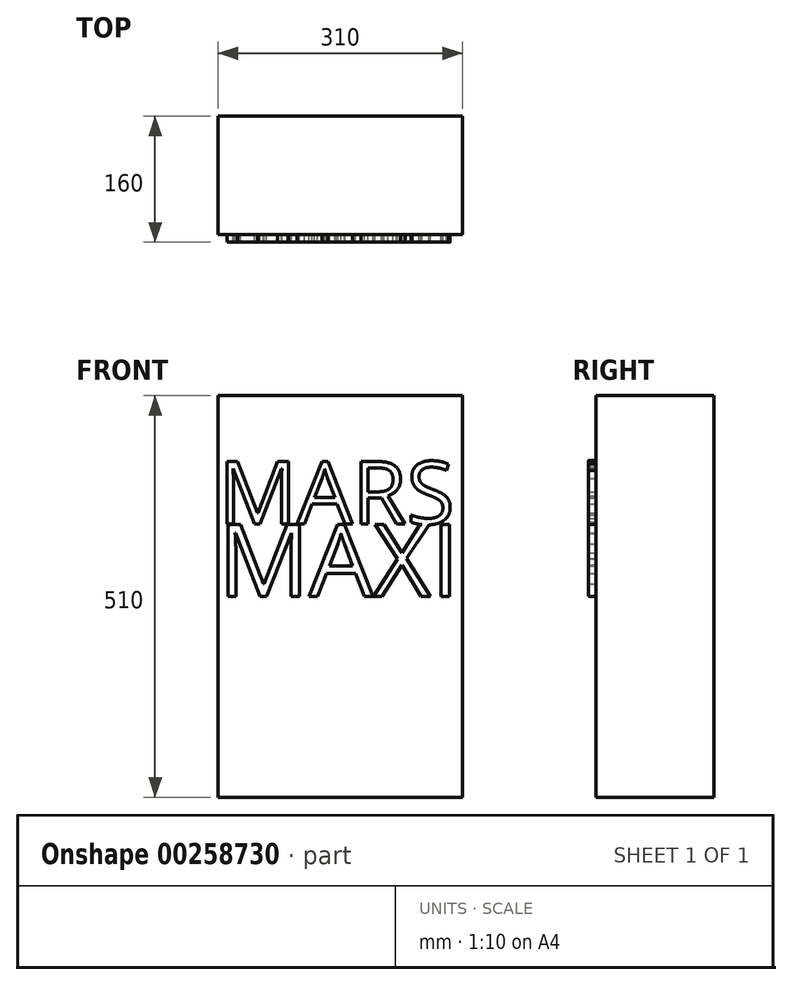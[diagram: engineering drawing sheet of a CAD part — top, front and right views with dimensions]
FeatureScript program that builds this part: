
annotation { "Feature Type Name" : "Feature", "Feature Type Description" : "" }
export const myFeature = defineFeature(function(context is Context, id is Id, definition is map)
    precondition{}
    {
        {
            var Q0;
            Q0=qCreatedBy(makeId("Front.planeOp"),FACE);
            var sketch = newSketch(context, id + "F0", { "sketchPlane" : qUnion([Q0])});
            skLineSegment(sketch, "E0.bottom", {"start": v(0, 0) * mm, "end": v(310, 0) * mm});
            skLineSegment(sketch, "E0.top", {"start": v(0, 510) * mm, "end": v(310, 510) * mm});
            skLineSegment(sketch, "E0.left", {"start": v(0, 0) * mm, "end": v(0, 510) * mm});
            skLineSegment(sketch, "E0.right", {"start": v(310, 0) * mm, "end": v(310, 510) * mm});
            skSolve(sketch);
        }
        {
            var Q0;
            Q0 = qSketchRegion(id + "F0", true);
            var Q1;
            Q1=makeQuery(id+"F0.imprint","IMPRINT",FACE,{"disambiguationData":[TD([[makeQuery(id+"F0.imprint","IMPRINT",EDGE,{"derivedFrom":sQuery(id+"F0.wireOp",EDGE,"E0.bottom")}),1.0]])]});
            extrude(context, id + "F2", {"entities" : qUnion([Q0, Q1]), "depth" : 150 * mm});
        }
        {
            var Q0;
            Q0=makeQuery(id+"F2.opExtrude","CAP_FACE",FACE,{"disambiguationData":[OSD([sQuery(id+"F0.wireOp",EDGE,"E0.bottom"),sQuery(id+"F0.wireOp",EDGE,"E0.top"),sQuery(id+"F0.wireOp",EDGE,"E0.left"),sQuery(id+"F0.wireOp",EDGE,"E0.right")])],"isStart":false});
            var sketch = newSketch(context, id + "F1", { "sketchPlane" : qUnion([Q0])});
            skText(sketch, "E1", { "text": "MARS", "fontName": "OpenSans-Regular.ttf"});
            skText(sketch, "E2", { "text": "MAXI", "fontName": "OpenSans-Regular.ttf"});
            const initialGuessF1  = {"E1": [0, 0.34716, 1, 0, 0.07993], "E2": [0, 0.255, 1, 0, 0.09216]};
            skSetInitialGuess(sketch, initialGuessF1);
            skSolve(sketch);
        }
        {
            var Q0;
            Q0 = qSketchRegion(id + "F1", true);
            extrude(context, id + "F3", {"entities" : qUnion([Q0]), "operationType" : NewBodyOperationType.ADD, "depth" : 10 * mm});
        }
    });
